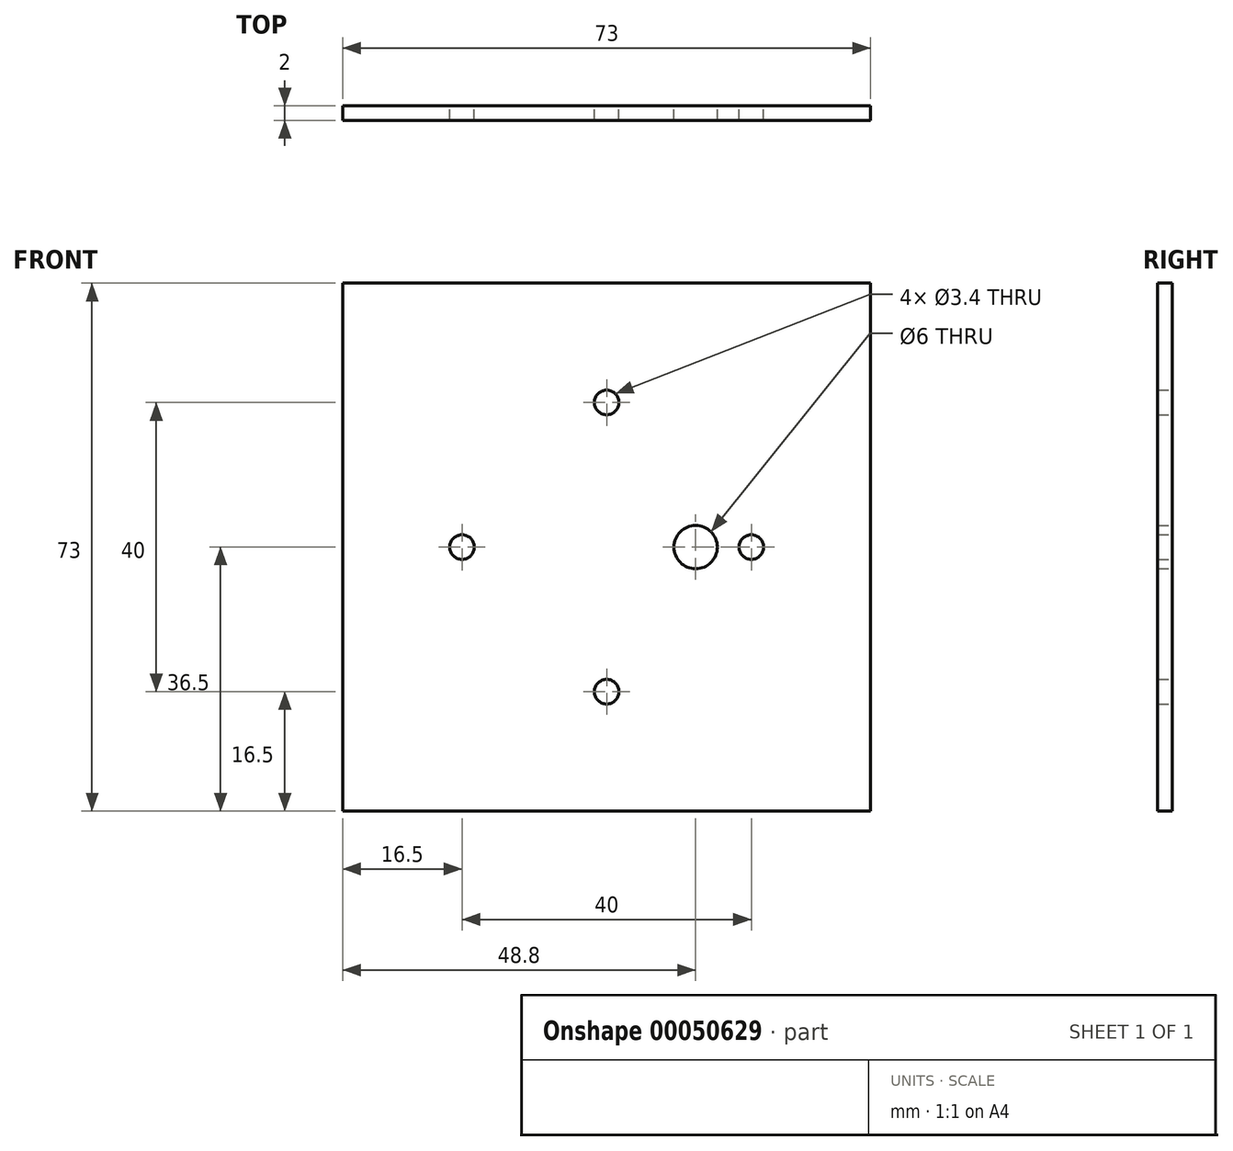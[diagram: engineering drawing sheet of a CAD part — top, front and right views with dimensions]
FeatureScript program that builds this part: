
annotation { "Feature Type Name" : "Feature", "Feature Type Description" : "" }
export const myFeature = defineFeature(function(context is Context, id is Id, definition is map)
    precondition{}
    {
        {
            var Q0;
            Q0=qCreatedBy(makeId("Front.planeOp"),FACE);
            var sketch = newSketch(context, id + "F0", { "sketchPlane" : qUnion([Q0])});
            skLineSegment(sketch, "E0", {"start": v(36.5, 0) * mm, "end": v(36.5, 36.5) * mm});
            skLineSegment(sketch, "E1", {"start": v(36.5, 36.5) * mm, "end": v(0, 36.5) * mm});
            skCircle(sketch, "E2", {"center": v(20, 0) * mm, "radius": 1.7 * mm});
            skCircle(sketch, "E3", {"center": v(0, 20) * mm, "radius": 1.7 * mm});
            skCircle(sketch, "E4", {"center": v(20, 20) * mm, "radius": 4 * mm, "construction": true});
            skCircle(sketch, "E5", {"center": v(12.3, 0) * mm, "radius": 3 * mm});
            skCircle(sketch, "E6.MirrorC", {"center": v(-20, 0) * mm, "radius": 1.7 * mm});
            skCircle(sketch, "E7.MirrorC", {"center": v(-20, 20) * mm, "radius": 4 * mm, "construction": true});
            skLineSegment(sketch, "E8.MirrorCS", {"start": v(-36.5, 36.5) * mm, "end": v(0, 36.5) * mm});
            skLineSegment(sketch, "E9.MirrorCS", {"start": v(-36.5, 0) * mm, "end": v(-36.5, 36.5) * mm});
            skCircle(sketch, "E10.MirrorC", {"center": v(0, -20) * mm, "radius": 1.7 * mm});
            skCircle(sketch, "E11.MirrorC", {"center": v(20, -20) * mm, "radius": 4 * mm, "construction": true});
            skLineSegment(sketch, "E12.MirrorCS", {"start": v(36.5, -36.5) * mm, "end": v(0, -36.5) * mm});
            skLineSegment(sketch, "E13.MirrorCS", {"start": v(36.5, 0) * mm, "end": v(36.5, -36.5) * mm});
            skLineSegment(sketch, "E14.MirrorCS", {"start": v(-36.5, -36.5) * mm, "end": v(0, -36.5) * mm});
            skLineSegment(sketch, "E15.MirrorCS", {"start": v(-36.5, 0) * mm, "end": v(-36.5, -36.5) * mm});
            skCircle(sketch, "E16.MirrorC", {"center": v(-20, -20) * mm, "radius": 4 * mm, "construction": true});
            skLineSegment(sketch, "E17.bottom", {"start": v(24, 16) * mm, "end": v(15.89, 16) * mm, "construction": true});
            skLineSegment(sketch, "E17.top", {"start": v(24, 24.04) * mm, "end": v(15.89, 24.04) * mm, "construction": true});
            skLineSegment(sketch, "E17.left", {"start": v(24, 16) * mm, "end": v(24, 24.04) * mm, "construction": true});
            skLineSegment(sketch, "E17.right", {"start": v(15.89, 16) * mm, "end": v(15.89, 24.04) * mm, "construction": true});
            skLineSegment(sketch, "E18.MirrorCS", {"start": v(-24, 16) * mm, "end": v(-15.89, 16) * mm, "construction": true});
            skLineSegment(sketch, "E19.MirrorCS", {"start": v(-15.89, 16) * mm, "end": v(-15.89, 24.04) * mm, "construction": true});
            skLineSegment(sketch, "E20.MirrorCS", {"start": v(-24, 16) * mm, "end": v(-24, 24.04) * mm, "construction": true});
            skLineSegment(sketch, "E21.MirrorCS", {"start": v(-24, 24.04) * mm, "end": v(-15.89, 24.04) * mm, "construction": true});
            skLineSegment(sketch, "E22.MirrorCS", {"start": v(24, -16) * mm, "end": v(15.89, -16) * mm, "construction": true});
            skLineSegment(sketch, "E23.MirrorCS", {"start": v(24, -16) * mm, "end": v(24, -24.04) * mm, "construction": true});
            skLineSegment(sketch, "E24.MirrorCS", {"start": v(24, -24.04) * mm, "end": v(15.89, -24.04) * mm, "construction": true});
            skLineSegment(sketch, "E25.MirrorCS", {"start": v(15.89, -16) * mm, "end": v(15.89, -24.04) * mm, "construction": true});
            skLineSegment(sketch, "E26.MirrorCS", {"start": v(-24, -16) * mm, "end": v(-15.89, -16) * mm, "construction": true});
            skLineSegment(sketch, "E27.MirrorCS", {"start": v(-24, -16) * mm, "end": v(-24, -24.04) * mm, "construction": true});
            skLineSegment(sketch, "E28.MirrorCS", {"start": v(-24, -24.04) * mm, "end": v(-15.89, -24.04) * mm, "construction": true});
            skLineSegment(sketch, "E29.MirrorCS", {"start": v(-15.89, -16) * mm, "end": v(-15.89, -24.04) * mm, "construction": true});
            skSolve(sketch);
        }
        {
            var Q0;
            Q0=qSketchRegion(id+"F0",true);
            extrude(context, id + "F1", {"entities" : qUnion([Q0]), "depth" : 2 * mm});
        }
    });
